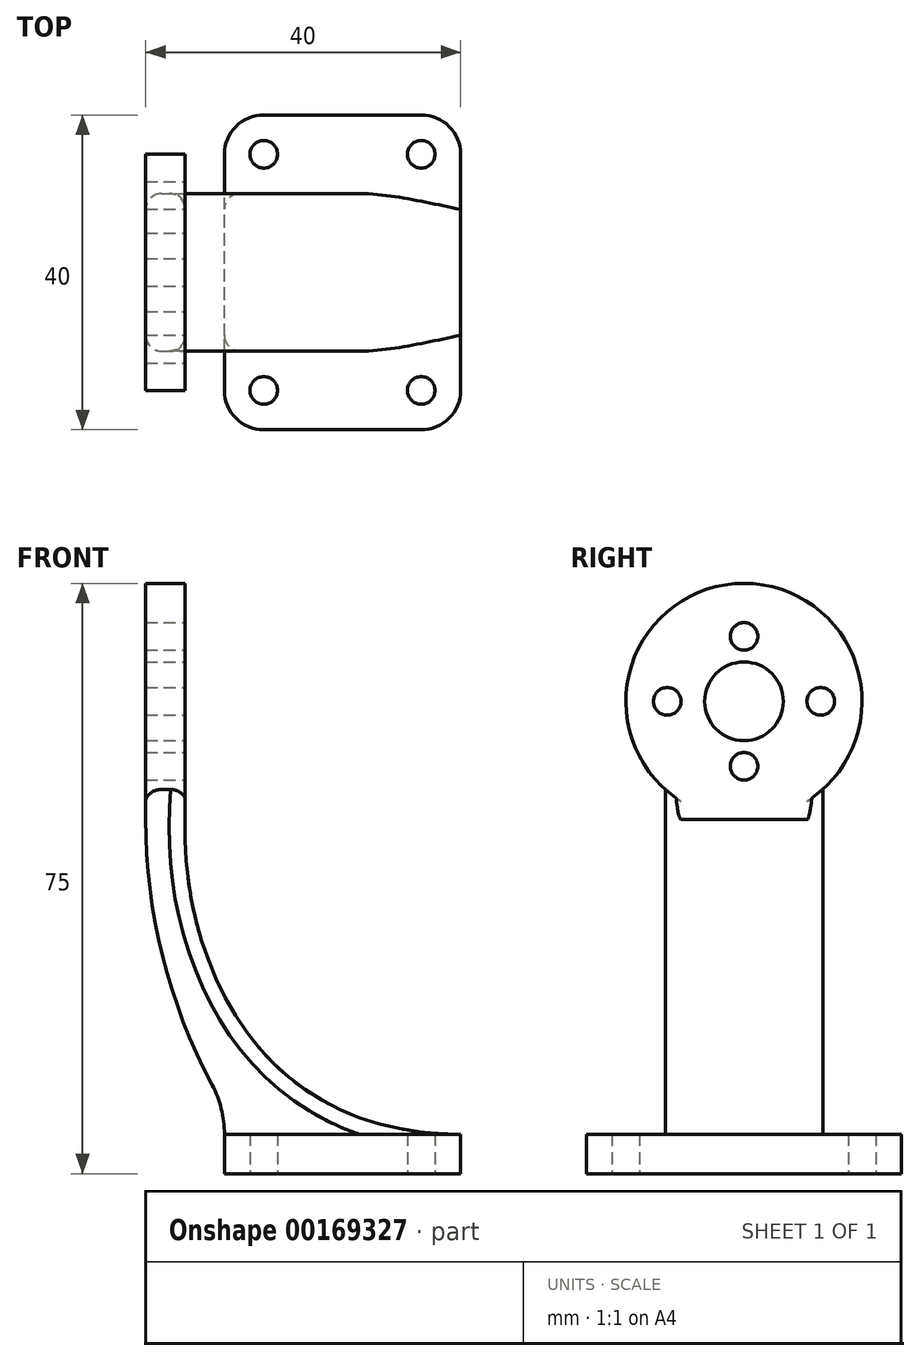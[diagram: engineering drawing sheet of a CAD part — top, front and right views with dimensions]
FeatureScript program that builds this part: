
annotation { "Feature Type Name" : "Feature", "Feature Type Description" : "" }
export const myFeature = defineFeature(function(context is Context, id is Id, definition is map)
    precondition{}
    {
        {
            var Q0;
            Q0=qCreatedBy(makeId("Front.planeOp"),FACE);
            var sketch = newSketch(context, id + "F0", { "sketchPlane" : qUnion([Q0])});
            skLineSegment(sketch, "E0.bottom", {"start": v(15, 2.5) * mm, "end": v(-15, 2.5) * mm});
            skLineSegment(sketch, "E0.top", {"start": v(15, -2.5) * mm, "end": v(-15, -2.5) * mm});
            skLineSegment(sketch, "E0.left", {"start": v(15, 2.5) * mm, "end": v(15, -2.5) * mm});
            skLineSegment(sketch, "E0.right", {"start": v(-15, 2.5) * mm, "end": v(-15, -2.5) * mm});
            skPoint(sketch, "E0.middle", {"position": v(0, 0) * mm});
            skLineSegment(sketch, "E1.bottom", {"start": v(-20, 42.5) * mm, "end": v(-25, 42.5) * mm});
            skLineSegment(sketch, "E1.top", {"start": v(-20, 57.5) * mm, "end": v(-25, 57.5) * mm});
            skLineSegment(sketch, "E1.left", {"start": v(-20, 42.5) * mm, "end": v(-20, 57.5) * mm});
            skLineSegment(sketch, "E1.right", {"start": v(-25, 42.5) * mm, "end": v(-25, 57.5) * mm});
            skPoint(sketch, "E1.middle", {"position": v(-22.5, 50) * mm});
            skArc(sketch, "E2", {"start": v(-25, 42.5) * mm, "mid": v(-22.86, 25.13) * mm, "end": v(-16.58, 8.8) * mm});
            skArc(sketch, "E3", {"start": v(-15, 2.5) * mm, "mid": v(-15.4, 5.75) * mm, "end": v(-16.58, 8.8) * mm});
            skFitSpline(sketch, "E4", {"points": [v(15, 2.5) * mm, v(-20, 42.5) * mm], "startDerivative": vector(-83.3, 0) * mm, "endDerivative": vector(1.64, 45.07) * mm});
            skSolve(sketch);
        }
        {
            var Q0;
            Q0=makeQuery(id+"F0.imprint","IMPRINT",FACE,{"disambiguationData":[TD([[makeQuery(id+"F0.imprint","IMPRINT",EDGE,{"derivedFrom":sQuery(id+"F0.wireOp",EDGE,"E1.bottom")}),-1.0]])]});
            var Q1;
            Q1=sQuery(id+"F0.wireOp",EDGE,"E1.top");
            revolve(context, id + "F1", {"entities" : qUnion([Q0]), "axis" : qUnion([Q1]), "revolveType" : RevolveType.FULL});
        }
        {
            var Q0;
            Q0=makeQuery(id+"F0.imprint","IMPRINT",FACE,{"disambiguationData":[TD([[makeQuery(id+"F0.imprint","IMPRINT",EDGE,{"derivedFrom":sQuery(id+"F0.wireOp",EDGE,"E0.bottom")}),1.0]])]});
            extrude(context, id + "F2", {"entities" : qUnion([Q0]), "endBound" : BoundingType.SYMMETRIC, "depth" : 40 * mm});
        }
        {
            var Q0;
            Q0=makeQuery(id+"F0.imprint","IMPRINT",FACE,{"disambiguationData":[TD([[makeQuery(id+"F0.imprint","IMPRINT",EDGE,{"derivedFrom":sQuery(id+"F0.wireOp",EDGE,"E0.bottom")}),-1.0]])]});
            var Q1;
            Q1=makeQuery(id+"F0.imprint","IMPRINT",FACE,{"disambiguationData":[TD([[makeQuery(id+"F0.imprint","IMPRINT",EDGE,{"derivedFrom":sQuery(id+"F0.wireOp",EDGE,"E1.bottom")}),-1.0]])]});
            extrude(context, id + "F3", {"entities" : qUnion([Q0, Q1]), "endBound" : BoundingType.SYMMETRIC, "depth" : 20 * mm});
        }
        {
            var Q0;
            Q0=makeQuery(id+"F2.opExtrude","SWEPT_BODY",BODY,{"disambiguationData":[OSD([sQuery(id+"F0.wireOp",EDGE,"E0.bottom"),sQuery(id+"F0.wireOp",EDGE,"E0.top"),sQuery(id+"F0.wireOp",EDGE,"E0.left"),sQuery(id+"F0.wireOp",EDGE,"E0.right")])]});
            var Q1;
            Q1=makeQuery(id+"F3.opExtrude","SWEPT_BODY",BODY,{"disambiguationData":[OSD([sQuery(id+"F0.wireOp",EDGE,"E0.bottom"),sQuery(id+"F0.wireOp",EDGE,"E1.top"),sQuery(id+"F0.wireOp",EDGE,"E1.left"),sQuery(id+"F0.wireOp",EDGE,"E1.right"),sQuery(id+"F0.wireOp",EDGE,"E2"),sQuery(id+"F0.wireOp",EDGE,"E3"),sQuery(id+"F0.wireOp",EDGE,"E4")])]});
            var Q2;
            Q2=makeQuery(id+"F1.opRevolve","SWEPT_BODY",BODY,{"disambiguationData":[OSD([sQuery(id+"F0.wireOp",EDGE,"E1.bottom"),sQuery(id+"F0.wireOp",EDGE,"E1.top"),sQuery(id+"F0.wireOp",EDGE,"E1.left"),sQuery(id+"F0.wireOp",EDGE,"E1.right")])]});
            booleanBodies(context, id + "F4", {"operationType" : BooleanOperationType.UNION, "tools" : qUnion([Q0, Q1, Q2])});
        }
        {
            var Q0;
            Q0=makeQuery(id+"F2.opExtrude","CAP_EDGE",EDGE,{"disambiguationData":[OSD([sQuery(id+"F0.wireOp",EDGE,"E0.left")])],"isStart":false});
            var Q1;
            Q1=makeQuery(id+"F2.opExtrude","CAP_EDGE",EDGE,{"disambiguationData":[OSD([sQuery(id+"F0.wireOp",EDGE,"E0.right")])],"isStart":false});
            var Q2;
            Q2=makeQuery(id+"F2.opExtrude","CAP_EDGE",EDGE,{"disambiguationData":[OSD([sQuery(id+"F0.wireOp",EDGE,"E0.right")])],"isStart":true});
            var Q3;
            Q3=makeQuery(id+"F2.opExtrude","CAP_EDGE",EDGE,{"disambiguationData":[OSD([sQuery(id+"F0.wireOp",EDGE,"E0.left")])],"isStart":true});
            fillet(context, id + "F5", {"entities" : qUnion([Q0, Q1, Q2, Q3]), "radius" : 5 * mm, "tangentPropagation" : true, "allowEdgeOverflow" : false});
        }
        {
            var Q0;
            Q0=makeQuery(id+"F3.opExtrude","CAP_EDGE",EDGE,{"disambiguationData":[OSD([sQuery(id+"F0.wireOp",EDGE,"E4")])],"isStart":true});
            var Q1;
            Q1=makeQuery(id+"F3.opExtrude","CAP_EDGE",EDGE,{"disambiguationData":[OSD([sQuery(id+"F0.wireOp",EDGE,"E4")])],"isStart":false});
            var Q2;
            Q2=makeQuery(id+"F3.opExtrude","CAP_EDGE",EDGE,{"disambiguationData":[OSD([sQuery(id+"F0.wireOp",EDGE,"E3")])],"isStart":true});
            var Q3;
            Q3=makeQuery(id+"F3.opExtrude","CAP_EDGE",EDGE,{"disambiguationData":[OSD([sQuery(id+"F0.wireOp",EDGE,"E2")])],"isStart":true});
            var Q4;
            Q4=makeQuery(id+"F3.opExtrude","CAP_EDGE",EDGE,{"disambiguationData":[OSD([sQuery(id+"F0.wireOp",EDGE,"E3")])],"isStart":false});
            fillet(context, id + "F6", {"entities" : qUnion([Q0, Q1, Q2, Q3, Q4]), "radius" : 2 * mm, "tangentPropagation" : true, "allowEdgeOverflow" : false});
        }
        {
            var Q0;
            {var subQ0=sQuery(id+"F0.wireOp",EDGE,"E1.left");Q0=makeQuery(id+"F4.opBoolean","MERGE",FACE,{"derivedFrom":[makeQuery(id+"F1.opRevolve","SWEPT_FACE",FACE,{"disambiguationData":[OSD([subQ0])]}),makeQuery(id+"F3.opExtrude","SWEPT_FACE",FACE,{"disambiguationData":[OSD([subQ0])]})]});}
            var sketch = newSketch(context, id + "F7", { "sketchPlane" : qUnion([Q0])});
            skCircle(sketch, "E5", {"center": v(0, 57.5) * mm, "radius": 5 * mm});
            skCircle(sketch, "E6", {"center": v(9.75, 57.5) * mm, "radius": 1.75 * mm});
            skCircle(sketch, "E7", {"center": v(0, 65.75) * mm, "radius": 1.75 * mm});
            skCircle(sketch, "E8", {"center": v(-9.75, 57.5) * mm, "radius": 1.75 * mm});
            skCircle(sketch, "E9", {"center": v(0, 49.25) * mm, "radius": 1.75 * mm});
            skSolve(sketch);
        }
        {
            var Q0;
            Q0=makeQuery(id+"F7.imprint","IMPRINT",FACE,{"disambiguationData":[TD([[makeQuery(id+"F7.imprint","IMPRINT",EDGE,{"derivedFrom":sQuery(id+"F7.wireOp",EDGE,"E8")}),1.0]])]});
            var Q1;
            Q1=makeQuery(id+"F7.imprint","IMPRINT",FACE,{"disambiguationData":[TD([[makeQuery(id+"F7.imprint","IMPRINT",EDGE,{"derivedFrom":sQuery(id+"F7.wireOp",EDGE,"E7")}),1.0]])]});
            var Q2;
            Q2=makeQuery(id+"F7.imprint","IMPRINT",FACE,{"disambiguationData":[TD([[makeQuery(id+"F7.imprint","IMPRINT",EDGE,{"derivedFrom":sQuery(id+"F7.wireOp",EDGE,"E6")}),1.0]])]});
            var Q3;
            Q3=makeQuery(id+"F7.imprint","IMPRINT",FACE,{"disambiguationData":[TD([[makeQuery(id+"F7.imprint","IMPRINT",EDGE,{"derivedFrom":sQuery(id+"F7.wireOp",EDGE,"E9")}),1.0]])]});
            var Q4;
            Q4=makeQuery(id+"F7.imprint","IMPRINT",FACE,{"disambiguationData":[TD([[makeQuery(id+"F7.imprint","IMPRINT",EDGE,{"derivedFrom":sQuery(id+"F7.wireOp",EDGE,"E5")}),1.0]])]});
            extrude(context, id + "F8", {"entities" : qUnion([Q0, Q1, Q2, Q3, Q4]), "operationType" : NewBodyOperationType.REMOVE, "oppositeDirection" : true, "depth" : 25 * mm});
        }
        {
            var Q0;
            Q0=makeQuery(id+"F2.opExtrude","SWEPT_FACE",FACE,{"disambiguationData":[OSD([sQuery(id+"F0.wireOp",EDGE,"E0.top")])]});
            var sketch = newSketch(context, id + "F9", { "sketchPlane" : qUnion([Q0])});
            skCircle(sketch, "E10", {"center": v(-10, -15) * mm, "radius": 1.75 * mm});
            skCircle(sketch, "E11", {"center": v(10, -15) * mm, "radius": 1.75 * mm});
            skCircle(sketch, "E12", {"center": v(10, 15) * mm, "radius": 1.75 * mm});
            skCircle(sketch, "E13", {"center": v(-10, 15) * mm, "radius": 1.75 * mm});
            skSolve(sketch);
        }
        {
            var Q0;
            Q0=makeQuery(id+"F9.imprint","IMPRINT",FACE,{"disambiguationData":[TD([[makeQuery(id+"F9.imprint","IMPRINT",EDGE,{"derivedFrom":sQuery(id+"F9.wireOp",EDGE,"E10")}),1.0]])]});
            var Q1;
            Q1=makeQuery(id+"F9.imprint","IMPRINT",FACE,{"disambiguationData":[TD([[makeQuery(id+"F9.imprint","IMPRINT",EDGE,{"derivedFrom":sQuery(id+"F9.wireOp",EDGE,"E13")}),1.0]])]});
            var Q2;
            Q2=makeQuery(id+"F9.imprint","IMPRINT",FACE,{"disambiguationData":[TD([[makeQuery(id+"F9.imprint","IMPRINT",EDGE,{"derivedFrom":sQuery(id+"F9.wireOp",EDGE,"E12")}),1.0]])]});
            var Q3;
            Q3=makeQuery(id+"F9.imprint","IMPRINT",FACE,{"disambiguationData":[TD([[makeQuery(id+"F9.imprint","IMPRINT",EDGE,{"derivedFrom":sQuery(id+"F9.wireOp",EDGE,"E11")}),1.0]])]});
            extrude(context, id + "F10", {"entities" : qUnion([Q0, Q1, Q2, Q3]), "operationType" : NewBodyOperationType.REMOVE, "oppositeDirection" : true, "depth" : 25 * mm});
        }
    });
